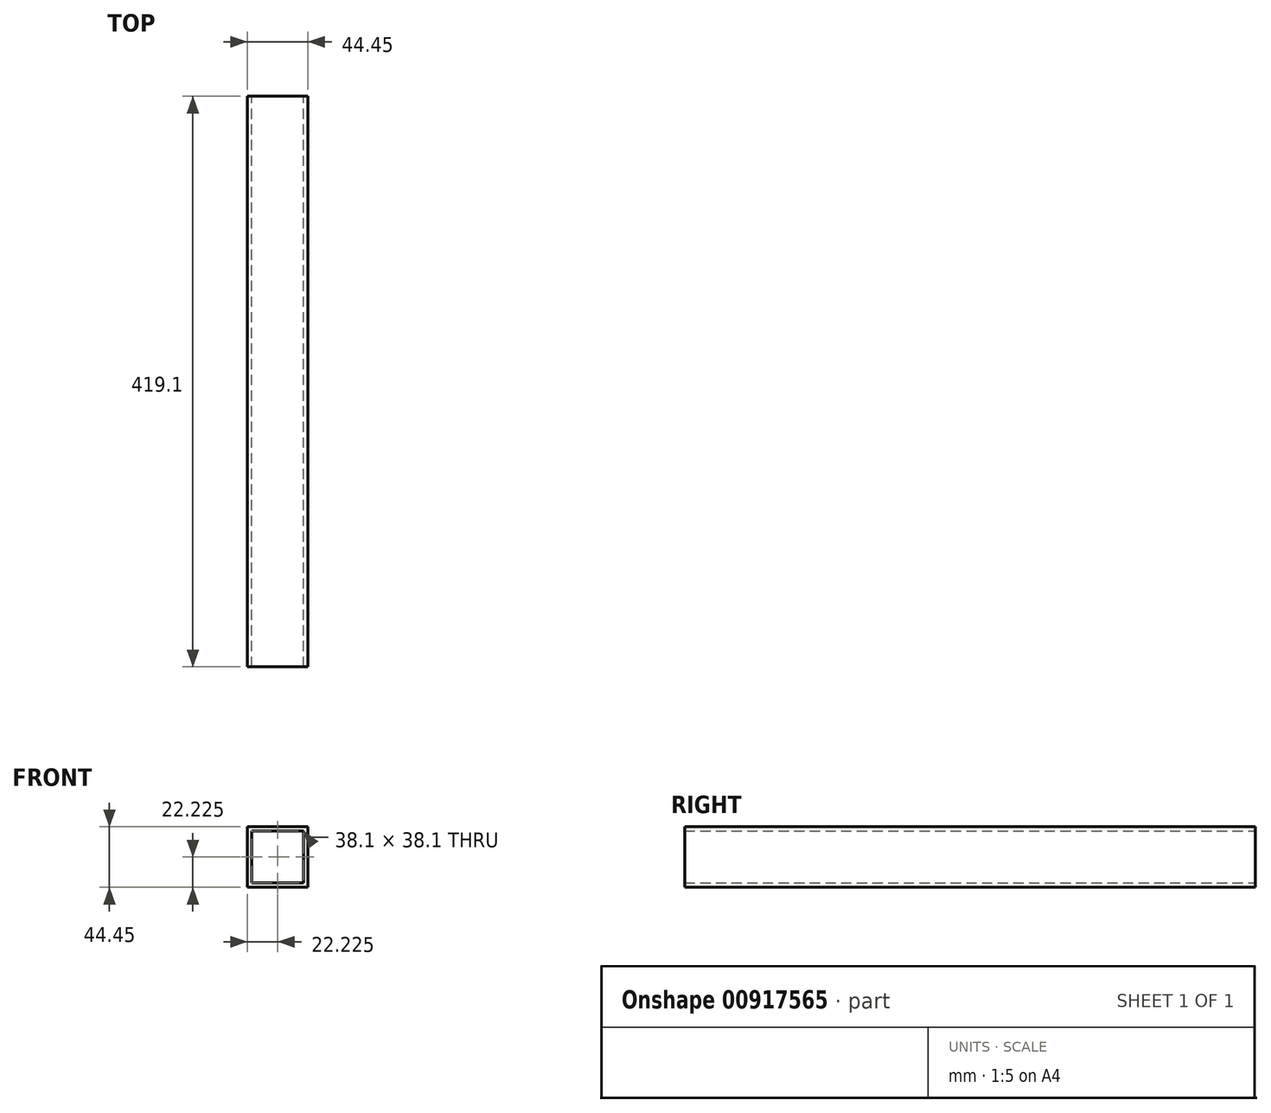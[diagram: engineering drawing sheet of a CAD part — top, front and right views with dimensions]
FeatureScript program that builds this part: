
annotation { "Feature Type Name" : "Feature", "Feature Type Description" : "" }
export const myFeature = defineFeature(function(context is Context, id is Id, definition is map)
    precondition{}
    {
        {
            var Q0;
            Q0=qCreatedBy(makeId("Front.planeOp"),FACE);
            var sketch = newSketch(context, id + "F0", { "sketchPlane" : qUnion([Q0])});
            skLineSegment(sketch, "E0.bottom", {"start": v(0, 0) * mm, "end": v(44.45, 0) * mm});
            skLineSegment(sketch, "E0.top", {"start": v(0, 44.45) * mm, "end": v(44.45, 44.45) * mm});
            skLineSegment(sketch, "E0.left", {"start": v(0, 0) * mm, "end": v(0, 44.45) * mm});
            skLineSegment(sketch, "E0.right", {"start": v(44.45, 0) * mm, "end": v(44.45, 44.45) * mm});
            skLineSegment(sketch, "E1.0", {"start": v(3.17, 41.28) * mm, "end": v(41.27, 41.28) * mm});
            skLineSegment(sketch, "E1.1", {"start": v(3.17, 3.17) * mm, "end": v(3.17, 41.28) * mm});
            skLineSegment(sketch, "E1.2", {"start": v(3.17, 3.17) * mm, "end": v(41.28, 3.17) * mm});
            skLineSegment(sketch, "E1.3", {"start": v(41.28, 3.17) * mm, "end": v(41.27, 41.28) * mm});
            skSolve(sketch);
        }
        {
            var Q0;
            Q0=makeQuery(id+"F0.imprint","IMPRINT",FACE,{"disambiguationData":[TD([[makeQuery(id+"F0.imprint","IMPRINT",EDGE,{"derivedFrom":sQuery(id+"F0.wireOp",EDGE,"E0.bottom")}),1.0]])]});
            extrude(context, id + "F1", {"entities" : qUnion([Q0]), "depth" : 419.1 * mm, "offsetDistance" : 25.4 * mm});
        }
    });
